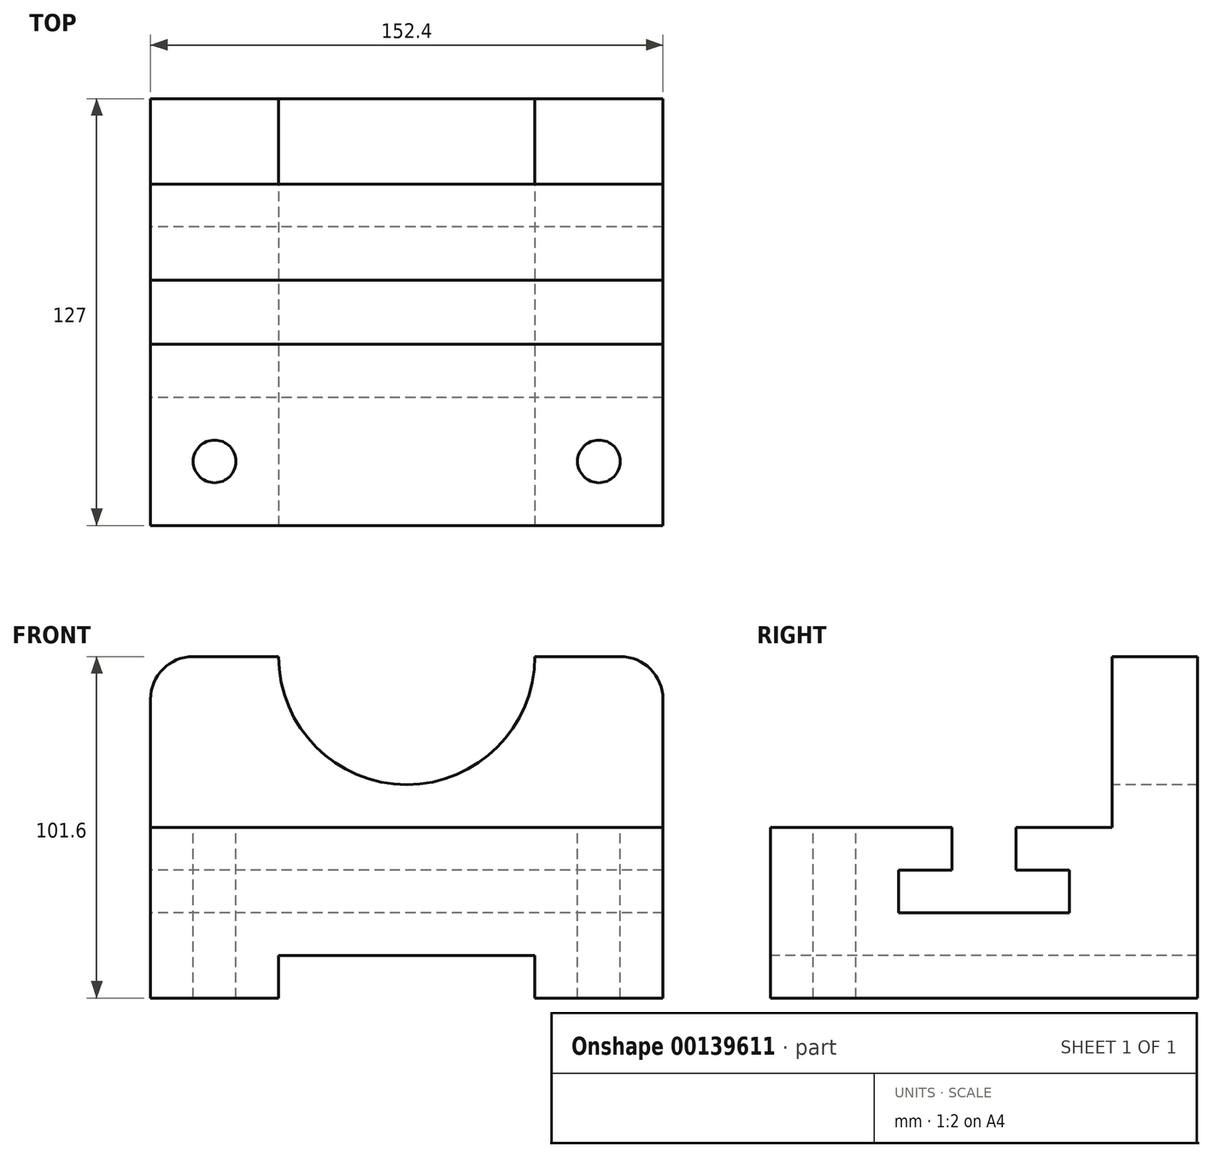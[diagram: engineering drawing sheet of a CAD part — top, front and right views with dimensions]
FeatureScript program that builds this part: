
annotation { "Feature Type Name" : "Feature", "Feature Type Description" : "" }
export const myFeature = defineFeature(function(context is Context, id is Id, definition is map)
    precondition{}
    {
        {
            var Q0;
            Q0=qCreatedBy(makeId("Right.planeOp"),FACE);
            var sketch = newSketch(context, id + "F0", { "sketchPlane" : qUnion([Q0])});
            skLineSegment(sketch, "E0", {"start": v(127, 101.6) * mm, "end": v(127, 0) * mm});
            skLineSegment(sketch, "E1", {"start": v(127, 0) * mm, "end": v(0, 0) * mm});
            skLineSegment(sketch, "E2", {"start": v(0, 0) * mm, "end": v(0, 50.8) * mm});
            skLineSegment(sketch, "E3", {"start": v(0, 50.8) * mm, "end": v(53.97, 50.8) * mm});
            skLineSegment(sketch, "E4", {"start": v(53.97, 50.8) * mm, "end": v(53.97, 38.1) * mm});
            skLineSegment(sketch, "E5", {"start": v(53.97, 38.1) * mm, "end": v(38.1, 38.1) * mm});
            skLineSegment(sketch, "E6", {"start": v(38.1, 38.1) * mm, "end": v(38.1, 25.4) * mm});
            skLineSegment(sketch, "E7", {"start": v(38.1, 25.4) * mm, "end": v(88.9, 25.4) * mm});
            skLineSegment(sketch, "E8", {"start": v(88.9, 25.4) * mm, "end": v(88.9, 38.1) * mm});
            skLineSegment(sketch, "E9", {"start": v(88.9, 38.1) * mm, "end": v(73.02, 38.1) * mm});
            skLineSegment(sketch, "E10", {"start": v(73.02, 38.1) * mm, "end": v(73.02, 50.8) * mm});
            skLineSegment(sketch, "E11", {"start": v(73.02, 50.8) * mm, "end": v(101.6, 50.8) * mm});
            skLineSegment(sketch, "E12", {"start": v(101.6, 50.8) * mm, "end": v(101.6, 101.6) * mm});
            skLineSegment(sketch, "E13", {"start": v(101.6, 101.6) * mm, "end": v(127, 101.6) * mm});
            skSolve(sketch);
        }
        {
            var Q0;
            Q0=makeQuery(id+"F0.imprint","IMPRINT",FACE,{"disambiguationData":[TD([[makeQuery(id+"F0.imprint","IMPRINT",EDGE,{"derivedFrom":sQuery(id+"F0.wireOp",EDGE,"E0")}),-1.0]])]});
            extrude(context, id + "F1", {"entities" : qUnion([Q0]), "depth" : 152.4 * mm});
        }
        {
            var Q0;
            Q0=makeQuery(id+"F1.opExtrude","SWEPT_FACE",FACE,{"disambiguationData":[OSD([sQuery(id+"F0.wireOp",EDGE,"E2")])]});
            var sketch = newSketch(context, id + "F2", { "sketchPlane" : qUnion([Q0])});
            skLineSegment(sketch, "E14", {"start": v(38.1, 0) * mm, "end": v(38.1, 12.7) * mm});
            skLineSegment(sketch, "E15", {"start": v(38.1, 12.7) * mm, "end": v(114.3, 12.7) * mm});
            skLineSegment(sketch, "E16", {"start": v(114.3, 12.7) * mm, "end": v(114.3, 0) * mm});
            skSolve(sketch);
        }
        {
            var Q0;
            {var subQ0=sQuery(id+"F2.wireOp",EDGE,"E14");Q0=makeQuery(id+"F2.imprint","IMPRINT",FACE,{"disambiguationData":[TD([[makeQuery(id+"F2.imprint","IMPRINT",EDGE,{"derivedFrom":subQ0}),-1.0]])]});}
            extrude(context, id + "F3", {"entities" : qUnion([Q0]), "operationType" : NewBodyOperationType.REMOVE, "endBound" : BoundingType.THROUGH_ALL, "oppositeDirection" : true, "depth" : 25.4 * mm});
        }
        {
            var Q0;
            Q0=makeQuery(id+"F1.opExtrude","SWEPT_FACE",FACE,{"disambiguationData":[OSD([sQuery(id+"F0.wireOp",EDGE,"E12")])]});
            var sketch = newSketch(context, id + "F4", { "sketchPlane" : qUnion([Q0])});
            skCircle(sketch, "E17", {"center": v(76.2, 101.6) * mm, "radius": 38.1 * mm});
            skSolve(sketch);
        }
        {
            var Q0;
            {var subQ0=sQuery(id+"F4.wireOp",EDGE,"E17");var subQ1=makeQuery(id+"F1.opExtrude","SWEPT_EDGE",EDGE,{"disambiguationData":[OSD([sQuery(id+"F0.wireOp",EDGE,"E12"),sQuery(id+"F0.wireOp",EDGE,"E13")])]});var subQ2=makeQuery(id+"F4.imprint","INTERSECT",VERTEX,{"disambiguationData":[OD(0.0)],"derivedFrom":[subQ1,subQ0]});Q0=makeQuery(id+"F4.imprint","IMPRINT",FACE,{"disambiguationData":[TD([[makeQuery(id+"F4.imprint","IMPRINT",EDGE,{"disambiguationData":[TD([[subQ2,-1.0]])],"derivedFrom":subQ0}),1.0]])]});}
            extrude(context, id + "F5", {"entities" : qUnion([Q0]), "operationType" : NewBodyOperationType.REMOVE, "oppositeDirection" : true, "depth" : 25.4 * mm});
        }
        {
            var Q0;
            Q0=makeQuery(id+"F1.opExtrude","CAP_EDGE",EDGE,{"disambiguationData":[OSD([sQuery(id+"F0.wireOp",EDGE,"E13")])],"isStart":true});
            var Q1;
            Q1=makeQuery(id+"F1.opExtrude","CAP_EDGE",EDGE,{"disambiguationData":[OSD([sQuery(id+"F0.wireOp",EDGE,"E13")])],"isStart":false});
            fillet(context, id + "F6", {"entities" : qUnion([Q0, Q1]), "radius" : 12.7 * mm, "tangentPropagation" : true, "allowEdgeOverflow" : false});
        }
        {
            var Q0;
            Q0=makeQuery(id+"F1.opExtrude","SWEPT_FACE",FACE,{"disambiguationData":[OSD([sQuery(id+"F0.wireOp",EDGE,"E3")])]});
            var sketch = newSketch(context, id + "F7", { "sketchPlane" : qUnion([Q0])});
            skCircle(sketch, "E18", {"center": v(19.05, 19.05) * mm, "radius": 6.35 * mm});
            skCircle(sketch, "E19", {"center": v(133.35, 19.05) * mm, "radius": 6.35 * mm});
            skSolve(sketch);
        }
        {
            var Q0;
            Q0=makeQuery(id+"F7.imprint","IMPRINT",FACE,{"disambiguationData":[TD([[makeQuery(id+"F7.imprint","IMPRINT",EDGE,{"derivedFrom":sQuery(id+"F7.wireOp",EDGE,"E18")}),1.0]])]});
            var Q1;
            Q1=makeQuery(id+"F7.imprint","IMPRINT",FACE,{"disambiguationData":[TD([[makeQuery(id+"F7.imprint","IMPRINT",EDGE,{"derivedFrom":sQuery(id+"F7.wireOp",EDGE,"E19")}),1.0]])]});
            extrude(context, id + "F8", {"entities" : qUnion([Q0, Q1]), "operationType" : NewBodyOperationType.REMOVE, "endBound" : BoundingType.THROUGH_ALL, "oppositeDirection" : true, "depth" : 25.4 * mm});
        }
    });
